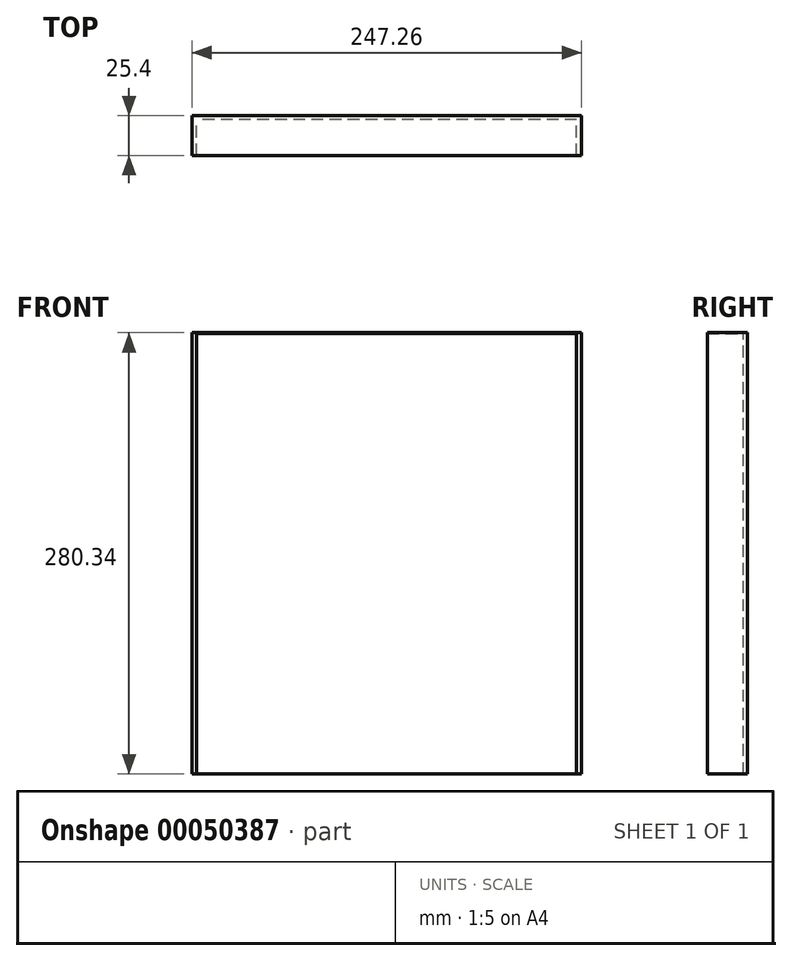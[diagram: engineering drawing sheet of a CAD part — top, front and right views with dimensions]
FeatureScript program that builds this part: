
annotation { "Feature Type Name" : "Feature", "Feature Type Description" : "" }
export const myFeature = defineFeature(function(context is Context, id is Id, definition is map)
    precondition{}
    {
        {
            var Q0;
            Q0=qCreatedBy(makeId("Front.planeOp"),FACE);
            var sketch = newSketch(context, id + "F0", { "sketchPlane" : qUnion([Q0])});
            skLineSegment(sketch, "E0.rect.top", {"start": v(120.65, 139.7) * mm, "end": v(-120.65, 139.7) * mm});
            skLineSegment(sketch, "E0.rect.left", {"start": v(120.65, -139.7) * mm, "end": v(120.65, 139.7) * mm});
            skLineSegment(sketch, "E0.rect.right", {"start": v(-120.65, -139.7) * mm, "end": v(-120.65, 139.7) * mm});
            skPoint(sketch, "E0.rect.middle", {"position": v(0, 0) * mm});
            skLineSegment(sketch, "E1.rect.bottom", {"start": v(123.63, -140.17) * mm, "end": v(-123.63, -140.17) * mm});
            skLineSegment(sketch, "E1.rect.top", {"start": v(123.63, 140.17) * mm, "end": v(-123.63, 140.17) * mm});
            skLineSegment(sketch, "E1.rect.left", {"start": v(123.63, -140.17) * mm, "end": v(123.63, 140.17) * mm});
            skLineSegment(sketch, "E1.rect.right", {"start": v(-123.63, -140.17) * mm, "end": v(-123.63, 140.17) * mm});
            skLineSegment(sketch, "E2", {"start": v(-120.65, -139.7) * mm, "end": v(-120.65, -140.17) * mm});
            skLineSegment(sketch, "E3", {"start": v(120.65, -139.7) * mm, "end": v(120.65, -140.17) * mm});
            skSolve(sketch);
        }
        {
            var Q0;
            Q0=makeQuery(id+"F0.imprint","IMPRINT",FACE,{"disambiguationData":[TD([[makeQuery(id+"F0.imprint","IMPRINT",EDGE,{"derivedFrom":sQuery(id+"F0.wireOp",EDGE,"E0.rect.top")}),-1.0]])]});
            extrude(context, id + "F1", {"entities" : qUnion([Q0]), "depth" : 25.4 * mm});
        }
        {
            var Q0;
            Q0=makeQuery(id+"F0.imprint","IMPRINT",FACE,{"disambiguationData":[TD([[makeQuery(id+"F0.imprint","IMPRINT",EDGE,{"derivedFrom":sQuery(id+"F0.wireOp",EDGE,"E0.rect.top")}),1.0]])]});
            extrude(context, id + "F2", {"entities" : qUnion([Q0]), "operationType" : NewBodyOperationType.ADD, "depth" : 2.54 * mm});
        }
    });
